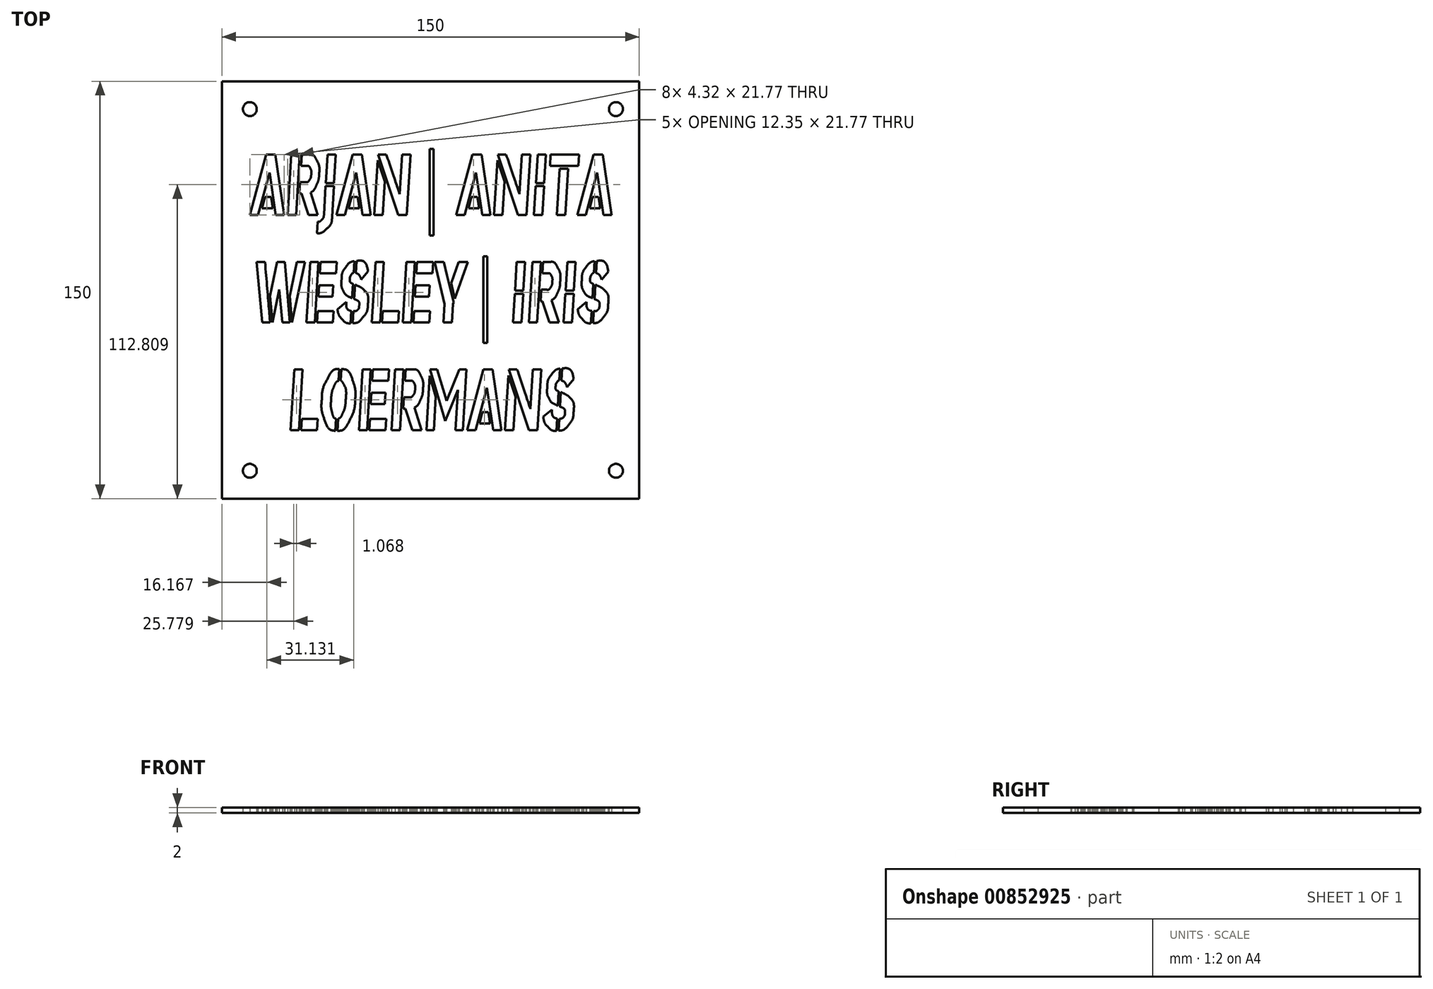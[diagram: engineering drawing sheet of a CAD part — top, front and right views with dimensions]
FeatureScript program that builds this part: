
annotation { "Feature Type Name" : "Feature", "Feature Type Description" : "" }
export const myFeature = defineFeature(function(context is Context, id is Id, definition is map)
    precondition{}
    {
        {
            var Q0;
            Q0=qCreatedBy(makeId("Top.planeOp"),FACE);
            var sketch = newSketch(context, id + "F0", { "sketchPlane" : qUnion([Q0])});
            skCircle(sketch, "E0", {"center": v(-65.05, 64.98) * mm, "radius": 2.5 * mm});
            skCircle(sketch, "E1", {"center": v(66.58, 64.98) * mm, "radius": 2.5 * mm});
            skCircle(sketch, "E2", {"center": v(-65.05, -65.02) * mm, "radius": 2.5 * mm});
            skCircle(sketch, "E3", {"center": v(66.58, -65.02) * mm, "radius": 2.5 * mm});
            skLineSegment(sketch, "E4.bottom", {"start": v(-75.05, 74.98) * mm, "end": v(74.95, 74.98) * mm});
            skLineSegment(sketch, "E4.top", {"start": v(-75.05, -75.02) * mm, "end": v(74.95, -75.02) * mm});
            skLineSegment(sketch, "E4.left", {"start": v(-75.05, 74.98) * mm, "end": v(-75.05, -75.02) * mm});
            skLineSegment(sketch, "E4.right", {"start": v(74.95, 74.98) * mm, "end": v(74.95, -75.02) * mm});
            skLineSegment(sketch, "E5", {"start": v(-62.06, 26.9) * mm, "end": v(-65.06, 26.9) * mm});
            skLineSegment(sketch, "E6", {"start": v(-65.06, 26.9) * mm, "end": v(-59.2, 48.68) * mm});
            skLineSegment(sketch, "E7", {"start": v(-59.2, 48.68) * mm, "end": v(-55.93, 48.68) * mm});
            skLineSegment(sketch, "E8", {"start": v(-55.93, 48.68) * mm, "end": v(-52.7, 26.9) * mm});
            skLineSegment(sketch, "E9", {"start": v(-52.7, 26.9) * mm, "end": v(-55.7, 26.9) * mm});
            skLineSegment(sketch, "E10", {"start": v(-55.7, 26.9) * mm, "end": v(-57.98, 42.11) * mm});
            skLineSegment(sketch, "E11", {"start": v(-57.98, 42.11) * mm, "end": v(-62.06, 26.9) * mm});
            skLineSegment(sketch, "E12", {"start": v(-60.66, 29.29) * mm, "end": v(-59.56, 33.36) * mm});
            skLineSegment(sketch, "E13", {"start": v(-59.56, 33.36) * mm, "end": v(-57.46, 33.36) * mm});
            skLineSegment(sketch, "E14", {"start": v(-57.46, 33.36) * mm, "end": v(-56.83, 29.29) * mm});
            skLineSegment(sketch, "E15", {"start": v(-56.83, 29.29) * mm, "end": v(-60.66, 29.29) * mm});
            skLineSegment(sketch, "E16", {"start": v(-40.6, 26.9) * mm, "end": v(-43.99, 26.9) * mm});
            skLineSegment(sketch, "E17", {"start": v(-43.99, 26.9) * mm, "end": v(-46.5, 34.62) * mm});
            skLineSegment(sketch, "E18", {"start": v(-46.5, 34.62) * mm, "end": v(-47.22, 34.62) * mm});
            skLineSegment(sketch, "E19", {"start": v(-47.22, 34.62) * mm, "end": v(-46.96, 38.7) * mm});
            skLineSegment(sketch, "E20", {"start": v(-46.96, 38.7) * mm, "end": v(-44.92, 38.7) * mm});
            skLineSegment(sketch, "E21", {"start": v(-44.57, 44.6) * mm, "end": v(-46.6, 44.6) * mm});
            skLineSegment(sketch, "E22", {"start": v(-46.6, 44.6) * mm, "end": v(-46.37, 48.68) * mm});
            skLineSegment(sketch, "E23", {"start": v(-46.37, 48.68) * mm, "end": v(-43.77, 48.68) * mm});
            skLineSegment(sketch, "E24", {"start": v(-43.23, 35) * mm, "end": v(-40.6, 26.9) * mm});
            skLineSegment(sketch, "E25", {"start": v(-48.43, 26.9) * mm, "end": v(-51.43, 26.9) * mm});
            skLineSegment(sketch, "E26", {"start": v(-51.43, 26.9) * mm, "end": v(-50.12, 48.68) * mm});
            skLineSegment(sketch, "E27", {"start": v(-50.12, 48.68) * mm, "end": v(-47.11, 48.68) * mm});
            skLineSegment(sketch, "E28", {"start": v(-47.11, 48.68) * mm, "end": v(-48.43, 26.9) * mm});
            skLineSegment(sketch, "E29", {"start": v(-34.77, 38.31) * mm, "end": v(-37.74, 38.31) * mm});
            skLineSegment(sketch, "E30", {"start": v(-37.74, 38.31) * mm, "end": v(-37.12, 48.7) * mm});
            skLineSegment(sketch, "E31", {"start": v(-37.12, 48.7) * mm, "end": v(-34.15, 48.7) * mm});
            skLineSegment(sketch, "E32", {"start": v(-34.15, 48.7) * mm, "end": v(-34.77, 38.31) * mm});
            skLineSegment(sketch, "E33", {"start": v(-34.83, 37.28) * mm, "end": v(-35.49, 26.3) * mm});
            skLineSegment(sketch, "E34", {"start": v(-40.93, 20.38) * mm, "end": v(-40.68, 24.52) * mm});
            skLineSegment(sketch, "E35", {"start": v(-38.42, 27.07) * mm, "end": v(-37.8, 37.28) * mm});
            skLineSegment(sketch, "E36", {"start": v(-37.8, 37.28) * mm, "end": v(-34.83, 37.28) * mm});
            skLineSegment(sketch, "E37", {"start": v(-30.93, 26.9) * mm, "end": v(-33.93, 26.9) * mm});
            skLineSegment(sketch, "E38", {"start": v(-33.93, 26.9) * mm, "end": v(-28.06, 48.68) * mm});
            skLineSegment(sketch, "E39", {"start": v(-28.06, 48.68) * mm, "end": v(-24.8, 48.68) * mm});
            skLineSegment(sketch, "E40", {"start": v(-24.8, 48.68) * mm, "end": v(-21.58, 26.9) * mm});
            skLineSegment(sketch, "E41", {"start": v(-21.58, 26.9) * mm, "end": v(-24.58, 26.9) * mm});
            skLineSegment(sketch, "E42", {"start": v(-24.58, 26.9) * mm, "end": v(-26.85, 42.11) * mm});
            skLineSegment(sketch, "E43", {"start": v(-26.85, 42.11) * mm, "end": v(-30.93, 26.9) * mm});
            skLineSegment(sketch, "E44", {"start": v(-29.53, 29.29) * mm, "end": v(-28.43, 33.36) * mm});
            skLineSegment(sketch, "E45", {"start": v(-28.43, 33.36) * mm, "end": v(-26.33, 33.36) * mm});
            skLineSegment(sketch, "E46", {"start": v(-26.33, 33.36) * mm, "end": v(-25.7, 29.29) * mm});
            skLineSegment(sketch, "E47", {"start": v(-25.7, 29.29) * mm, "end": v(-29.53, 29.29) * mm});
            skLineSegment(sketch, "E48", {"start": v(-16.57, 38.97) * mm, "end": v(-17.3, 26.9) * mm});
            skLineSegment(sketch, "E49", {"start": v(-17.3, 26.9) * mm, "end": v(-20.3, 26.9) * mm});
            skLineSegment(sketch, "E50", {"start": v(-20.3, 26.9) * mm, "end": v(-19.1, 46.56) * mm});
            skLineSegment(sketch, "E51", {"start": v(-19.1, 46.56) * mm, "end": v(-16.57, 38.97) * mm});
            skLineSegment(sketch, "E52", {"start": v(-8.62, 26.9) * mm, "end": v(-11.67, 26.9) * mm});
            skLineSegment(sketch, "E53", {"start": v(-11.67, 26.9) * mm, "end": v(-18.98, 48.68) * mm});
            skLineSegment(sketch, "E54", {"start": v(-18.98, 48.68) * mm, "end": v(-15.98, 48.68) * mm});
            skLineSegment(sketch, "E55", {"start": v(-11.17, 34.45) * mm, "end": v(-10.3, 48.68) * mm});
            skLineSegment(sketch, "E56", {"start": v(-10.3, 48.68) * mm, "end": v(-7.3, 48.68) * mm});
            skLineSegment(sketch, "E57", {"start": v(-7.3, 48.68) * mm, "end": v(-8.62, 26.9) * mm});
            skLineSegment(sketch, "E58", {"start": v(1.05, 50.68) * mm, "end": v(1.05, 19.56) * mm});
            skLineSegment(sketch, "E59", {"start": v(1.05, 19.56) * mm, "end": v(-0.43, 19.56) * mm});
            skLineSegment(sketch, "E60", {"start": v(-0.43, 19.56) * mm, "end": v(-0.43, 50.68) * mm});
            skLineSegment(sketch, "E61", {"start": v(-0.43, 50.68) * mm, "end": v(1.05, 50.68) * mm});
            skLineSegment(sketch, "E62", {"start": v(12.15, 26.9) * mm, "end": v(9.14, 26.9) * mm});
            skLineSegment(sketch, "E63", {"start": v(9.14, 26.9) * mm, "end": v(15, 48.68) * mm});
            skLineSegment(sketch, "E64", {"start": v(15, 48.68) * mm, "end": v(18.28, 48.68) * mm});
            skLineSegment(sketch, "E65", {"start": v(18.28, 48.68) * mm, "end": v(21.5, 26.9) * mm});
            skLineSegment(sketch, "E66", {"start": v(21.5, 26.9) * mm, "end": v(18.5, 26.9) * mm});
            skLineSegment(sketch, "E67", {"start": v(18.5, 26.9) * mm, "end": v(16.23, 42.11) * mm});
            skLineSegment(sketch, "E68", {"start": v(16.23, 42.11) * mm, "end": v(12.15, 26.9) * mm});
            skLineSegment(sketch, "E69", {"start": v(13.54, 29.29) * mm, "end": v(14.64, 33.36) * mm});
            skLineSegment(sketch, "E70", {"start": v(14.64, 33.36) * mm, "end": v(16.74, 33.36) * mm});
            skLineSegment(sketch, "E71", {"start": v(16.74, 33.36) * mm, "end": v(17.37, 29.29) * mm});
            skLineSegment(sketch, "E72", {"start": v(17.37, 29.29) * mm, "end": v(13.54, 29.29) * mm});
            skLineSegment(sketch, "E73", {"start": v(26.5, 38.97) * mm, "end": v(25.78, 26.9) * mm});
            skLineSegment(sketch, "E74", {"start": v(25.78, 26.9) * mm, "end": v(22.78, 26.9) * mm});
            skLineSegment(sketch, "E75", {"start": v(22.78, 26.9) * mm, "end": v(23.97, 46.56) * mm});
            skLineSegment(sketch, "E76", {"start": v(23.97, 46.56) * mm, "end": v(26.5, 38.97) * mm});
            skLineSegment(sketch, "E77", {"start": v(34.45, 26.9) * mm, "end": v(31.4, 26.9) * mm});
            skLineSegment(sketch, "E78", {"start": v(31.4, 26.9) * mm, "end": v(24.09, 48.68) * mm});
            skLineSegment(sketch, "E79", {"start": v(24.09, 48.68) * mm, "end": v(27.1, 48.68) * mm});
            skLineSegment(sketch, "E80", {"start": v(31.9, 34.45) * mm, "end": v(32.76, 48.68) * mm});
            skLineSegment(sketch, "E81", {"start": v(32.76, 48.68) * mm, "end": v(35.77, 48.68) * mm});
            skLineSegment(sketch, "E82", {"start": v(35.77, 48.68) * mm, "end": v(34.45, 26.9) * mm});
            skLineSegment(sketch, "E83", {"start": v(37.1, 26.9) * mm, "end": v(37.74, 37.28) * mm});
            skLineSegment(sketch, "E84", {"start": v(37.74, 37.28) * mm, "end": v(40.74, 37.28) * mm});
            skLineSegment(sketch, "E85", {"start": v(40.74, 37.28) * mm, "end": v(40.1, 26.9) * mm});
            skLineSegment(sketch, "E86", {"start": v(40.1, 26.9) * mm, "end": v(37.1, 26.9) * mm});
            skLineSegment(sketch, "E87", {"start": v(37.8, 38.31) * mm, "end": v(38.42, 48.68) * mm});
            skLineSegment(sketch, "E88", {"start": v(38.42, 48.68) * mm, "end": v(41.42, 48.68) * mm});
            skLineSegment(sketch, "E89", {"start": v(41.42, 48.68) * mm, "end": v(40.8, 38.31) * mm});
            skLineSegment(sketch, "E90", {"start": v(40.8, 38.31) * mm, "end": v(37.8, 38.31) * mm});
            skLineSegment(sketch, "E91", {"start": v(42.86, 44.6) * mm, "end": v(43.1, 48.68) * mm});
            skLineSegment(sketch, "E92", {"start": v(43.1, 48.68) * mm, "end": v(53.28, 48.68) * mm});
            skLineSegment(sketch, "E93", {"start": v(53.28, 48.68) * mm, "end": v(53.04, 44.6) * mm});
            skLineSegment(sketch, "E94", {"start": v(53.04, 44.6) * mm, "end": v(42.86, 44.6) * mm});
            skLineSegment(sketch, "E95", {"start": v(49.4, 43.52) * mm, "end": v(48.4, 26.9) * mm});
            skLineSegment(sketch, "E96", {"start": v(48.4, 26.9) * mm, "end": v(45.39, 26.9) * mm});
            skLineSegment(sketch, "E97", {"start": v(45.39, 26.9) * mm, "end": v(46.4, 43.52) * mm});
            skLineSegment(sketch, "E98", {"start": v(46.4, 43.52) * mm, "end": v(49.4, 43.52) * mm});
            skLineSegment(sketch, "E99", {"start": v(55.7, 26.9) * mm, "end": v(52.7, 26.9) * mm});
            skLineSegment(sketch, "E100", {"start": v(52.7, 26.9) * mm, "end": v(58.57, 48.68) * mm});
            skLineSegment(sketch, "E101", {"start": v(58.57, 48.68) * mm, "end": v(61.84, 48.68) * mm});
            skLineSegment(sketch, "E102", {"start": v(61.84, 48.68) * mm, "end": v(65.06, 26.9) * mm});
            skLineSegment(sketch, "E103", {"start": v(65.06, 26.9) * mm, "end": v(62.06, 26.9) * mm});
            skLineSegment(sketch, "E104", {"start": v(62.06, 26.9) * mm, "end": v(59.79, 42.11) * mm});
            skLineSegment(sketch, "E105", {"start": v(59.79, 42.11) * mm, "end": v(55.7, 26.9) * mm});
            skLineSegment(sketch, "E106", {"start": v(57.1, 29.29) * mm, "end": v(58.2, 33.36) * mm});
            skLineSegment(sketch, "E107", {"start": v(58.2, 33.36) * mm, "end": v(60.3, 33.36) * mm});
            skLineSegment(sketch, "E108", {"start": v(60.3, 33.36) * mm, "end": v(60.94, 29.29) * mm});
            skLineSegment(sketch, "E109", {"start": v(60.94, 29.29) * mm, "end": v(57.1, 29.29) * mm});
            skLineSegment(sketch, "E110", {"start": v(-50.63, -2.18) * mm, "end": v(-48.13, 10.04) * mm});
            skLineSegment(sketch, "E111", {"start": v(-48.13, 10.04) * mm, "end": v(-45.17, 10.04) * mm});
            skLineSegment(sketch, "E112", {"start": v(-45.17, 10.04) * mm, "end": v(-49.86, -11.74) * mm});
            skLineSegment(sketch, "E113", {"start": v(-49.86, -11.74) * mm, "end": v(-50.63, -2.18) * mm});
            skLineSegment(sketch, "E114", {"start": v(-50.61, -11.74) * mm, "end": v(-53.35, -11.74) * mm});
            skLineSegment(sketch, "E115", {"start": v(-53.35, -11.74) * mm, "end": v(-54.45, 0.05) * mm});
            skLineSegment(sketch, "E116", {"start": v(-54.45, 0.05) * mm, "end": v(-56.95, -11.74) * mm});
            skLineSegment(sketch, "E117", {"start": v(-56.95, -11.74) * mm, "end": v(-57.81, -2.18) * mm});
            skLineSegment(sketch, "E118", {"start": v(-57.81, -2.18) * mm, "end": v(-55.27, 10.04) * mm});
            skLineSegment(sketch, "E119", {"start": v(-55.27, 10.04) * mm, "end": v(-52.45, 10.04) * mm});
            skLineSegment(sketch, "E120", {"start": v(-52.45, 10.04) * mm, "end": v(-50.61, -11.74) * mm});
            skLineSegment(sketch, "E121", {"start": v(-60.52, -11.74) * mm, "end": v(-62.56, 10.04) * mm});
            skLineSegment(sketch, "E122", {"start": v(-62.56, 10.04) * mm, "end": v(-59.6, 10.04) * mm});
            skLineSegment(sketch, "E123", {"start": v(-57.78, -11.74) * mm, "end": v(-60.52, -11.74) * mm});
            skLineSegment(sketch, "E124", {"start": v(-41.68, -11.74) * mm, "end": v(-44.69, -11.74) * mm});
            skLineSegment(sketch, "E125", {"start": v(-44.69, -11.74) * mm, "end": v(-43.37, 10.04) * mm});
            skLineSegment(sketch, "E126", {"start": v(-43.37, 10.04) * mm, "end": v(-40.37, 10.04) * mm});
            skLineSegment(sketch, "E127", {"start": v(-40.37, 10.04) * mm, "end": v(-41.68, -11.74) * mm});
            skLineSegment(sketch, "E128", {"start": v(-40.13, 1.62) * mm, "end": v(-35.1, 1.62) * mm});
            skLineSegment(sketch, "E129", {"start": v(-35.1, 1.62) * mm, "end": v(-35.35, -2.45) * mm});
            skLineSegment(sketch, "E130", {"start": v(-35.35, -2.45) * mm, "end": v(-40.38, -2.45) * mm});
            skLineSegment(sketch, "E131", {"start": v(-40.38, -2.45) * mm, "end": v(-40.13, 1.62) * mm});
            skLineSegment(sketch, "E132", {"start": v(-40.7, -7.67) * mm, "end": v(-34.9, -7.67) * mm});
            skLineSegment(sketch, "E133", {"start": v(-34.9, -7.67) * mm, "end": v(-35.15, -11.74) * mm});
            skLineSegment(sketch, "E134", {"start": v(-35.15, -11.74) * mm, "end": v(-40.94, -11.74) * mm});
            skLineSegment(sketch, "E135", {"start": v(-40.94, -11.74) * mm, "end": v(-40.7, -7.67) * mm});
            skLineSegment(sketch, "E136", {"start": v(-39.63, 10.04) * mm, "end": v(-33.83, 10.04) * mm});
            skLineSegment(sketch, "E137", {"start": v(-33.83, 10.04) * mm, "end": v(-34.08, 5.96) * mm});
            skLineSegment(sketch, "E138", {"start": v(-34.08, 5.96) * mm, "end": v(-39.86, 5.96) * mm});
            skLineSegment(sketch, "E139", {"start": v(-39.86, 5.96) * mm, "end": v(-39.63, 10.04) * mm});
            skLineSegment(sketch, "E140", {"start": v(-27.95, 2.2) * mm, "end": v(-28.26, -2.97) * mm});
            skLineSegment(sketch, "E141", {"start": v(-27.45, 10.34) * mm, "end": v(-27.7, 6.1) * mm});
            skLineSegment(sketch, "E142", {"start": v(-26.7, 10.4) * mm, "end": v(-26.57, 10.4) * mm});
            skLineSegment(sketch, "E143", {"start": v(-22.56, 6.59) * mm, "end": v(-24.99, 3.72) * mm});
            skLineSegment(sketch, "E144", {"start": v(-26.96, 6.06) * mm, "end": v(-26.7, 10.4) * mm});
            skLineSegment(sketch, "E145", {"start": v(-27.21, 1.86) * mm, "end": v(-26.92, 1.76) * mm});
            skLineSegment(sketch, "E146", {"start": v(-28.04, -11.98) * mm, "end": v(-27.8, -7.7) * mm});
            skLineSegment(sketch, "E147", {"start": v(-27.8, -7.7) * mm, "end": v(-27.53, -7.7) * mm});
            skLineSegment(sketch, "E148", {"start": v(-27.51, -3.29) * mm, "end": v(-27.21, 1.86) * mm});
            skLineSegment(sketch, "E149", {"start": v(-33.53, -6.98) * mm, "end": v(-30.37, -4.38) * mm});
            skLineSegment(sketch, "E150", {"start": v(-28.54, -7.59) * mm, "end": v(-28.8, -12.04) * mm});
            skLineSegment(sketch, "E151", {"start": v(-17.23, -7.67) * mm, "end": v(-11.46, -7.67) * mm});
            skLineSegment(sketch, "E152", {"start": v(-11.46, -7.67) * mm, "end": v(-11.7, -11.74) * mm});
            skLineSegment(sketch, "E153", {"start": v(-11.7, -11.74) * mm, "end": v(-17.47, -11.74) * mm});
            skLineSegment(sketch, "E154", {"start": v(-17.47, -11.74) * mm, "end": v(-17.23, -7.67) * mm});
            skLineSegment(sketch, "E155", {"start": v(-18.19, -11.74) * mm, "end": v(-21.2, -11.74) * mm});
            skLineSegment(sketch, "E156", {"start": v(-21.2, -11.74) * mm, "end": v(-19.88, 10.04) * mm});
            skLineSegment(sketch, "E157", {"start": v(-19.88, 10.04) * mm, "end": v(-16.87, 10.04) * mm});
            skLineSegment(sketch, "E158", {"start": v(-16.87, 10.04) * mm, "end": v(-18.19, -11.74) * mm});
            skLineSegment(sketch, "E159", {"start": v(-7.02, -11.74) * mm, "end": v(-10.02, -11.74) * mm});
            skLineSegment(sketch, "E160", {"start": v(-10.02, -11.74) * mm, "end": v(-8.7, 10.04) * mm});
            skLineSegment(sketch, "E161", {"start": v(-8.7, 10.04) * mm, "end": v(-5.7, 10.04) * mm});
            skLineSegment(sketch, "E162", {"start": v(-5.7, 10.04) * mm, "end": v(-7.02, -11.74) * mm});
            skLineSegment(sketch, "E163", {"start": v(-5.46, 1.62) * mm, "end": v(-0.42, 1.62) * mm});
            skLineSegment(sketch, "E164", {"start": v(-0.42, 1.62) * mm, "end": v(-0.68, -2.45) * mm});
            skLineSegment(sketch, "E165", {"start": v(-0.68, -2.45) * mm, "end": v(-5.71, -2.45) * mm});
            skLineSegment(sketch, "E166", {"start": v(-5.71, -2.45) * mm, "end": v(-5.46, 1.62) * mm});
            skLineSegment(sketch, "E167", {"start": v(-6.03, -7.67) * mm, "end": v(-0.24, -7.67) * mm});
            skLineSegment(sketch, "E168", {"start": v(-0.24, -7.67) * mm, "end": v(-0.48, -11.74) * mm});
            skLineSegment(sketch, "E169", {"start": v(-0.48, -11.74) * mm, "end": v(-6.27, -11.74) * mm});
            skLineSegment(sketch, "E170", {"start": v(-6.27, -11.74) * mm, "end": v(-6.03, -7.67) * mm});
            skLineSegment(sketch, "E171", {"start": v(-4.96, 10.04) * mm, "end": v(0.84, 10.04) * mm});
            skLineSegment(sketch, "E172", {"start": v(0.84, 10.04) * mm, "end": v(0.6, 5.96) * mm});
            skLineSegment(sketch, "E173", {"start": v(0.6, 5.96) * mm, "end": v(-5.2, 5.96) * mm});
            skLineSegment(sketch, "E174", {"start": v(-5.2, 5.96) * mm, "end": v(-4.96, 10.04) * mm});
            skLineSegment(sketch, "E175", {"start": v(5, -5.14) * mm, "end": v(1.41, 10.04) * mm});
            skLineSegment(sketch, "E176", {"start": v(1.41, 10.04) * mm, "end": v(4.68, 10.04) * mm});
            skLineSegment(sketch, "E177", {"start": v(4.68, 10.04) * mm, "end": v(5.83, 5.23) * mm});
            skLineSegment(sketch, "E178", {"start": v(5.83, 5.23) * mm, "end": v(8.2, -4.5) * mm});
            skLineSegment(sketch, "E179", {"start": v(8.2, -4.5) * mm, "end": v(7.97, -5.14) * mm});
            skLineSegment(sketch, "E180", {"start": v(7.97, -5.14) * mm, "end": v(7.57, -11.74) * mm});
            skLineSegment(sketch, "E181", {"start": v(7.57, -11.74) * mm, "end": v(4.6, -11.74) * mm});
            skLineSegment(sketch, "E182", {"start": v(4.6, -11.74) * mm, "end": v(5, -5.14) * mm});
            skLineSegment(sketch, "E183", {"start": v(7.34, 2.36) * mm, "end": v(10.09, 10.04) * mm});
            skLineSegment(sketch, "E184", {"start": v(10.09, 10.04) * mm, "end": v(13.4, 10.04) * mm});
            skLineSegment(sketch, "E185", {"start": v(13.4, 10.04) * mm, "end": v(8.65, -3.2) * mm});
            skLineSegment(sketch, "E186", {"start": v(8.65, -3.2) * mm, "end": v(7.34, 2.36) * mm});
            skLineSegment(sketch, "E187", {"start": v(20.37, 12.04) * mm, "end": v(20.37, -19.08) * mm});
            skLineSegment(sketch, "E188", {"start": v(20.37, -19.08) * mm, "end": v(18.88, -19.08) * mm});
            skLineSegment(sketch, "E189", {"start": v(18.88, -19.08) * mm, "end": v(18.88, 12.04) * mm});
            skLineSegment(sketch, "E190", {"start": v(18.88, 12.04) * mm, "end": v(20.37, 12.04) * mm});
            skLineSegment(sketch, "E191", {"start": v(29.6, -11.74) * mm, "end": v(30.23, -1.36) * mm});
            skLineSegment(sketch, "E192", {"start": v(30.23, -1.36) * mm, "end": v(33.23, -1.36) * mm});
            skLineSegment(sketch, "E193", {"start": v(33.23, -1.36) * mm, "end": v(32.6, -11.74) * mm});
            skLineSegment(sketch, "E194", {"start": v(32.6, -11.74) * mm, "end": v(29.6, -11.74) * mm});
            skLineSegment(sketch, "E195", {"start": v(30.29, -0.33) * mm, "end": v(30.9, 10.04) * mm});
            skLineSegment(sketch, "E196", {"start": v(30.9, 10.04) * mm, "end": v(33.91, 10.04) * mm});
            skLineSegment(sketch, "E197", {"start": v(33.91, 10.04) * mm, "end": v(33.29, -0.33) * mm});
            skLineSegment(sketch, "E198", {"start": v(33.29, -0.33) * mm, "end": v(30.29, -0.33) * mm});
            skLineSegment(sketch, "E199", {"start": v(46.08, -11.74) * mm, "end": v(42.7, -11.74) * mm});
            skLineSegment(sketch, "E200", {"start": v(42.7, -11.74) * mm, "end": v(40.19, -4.02) * mm});
            skLineSegment(sketch, "E201", {"start": v(40.19, -4.02) * mm, "end": v(39.47, -4.02) * mm});
            skLineSegment(sketch, "E202", {"start": v(39.47, -4.02) * mm, "end": v(39.72, 0.05) * mm});
            skLineSegment(sketch, "E203", {"start": v(39.72, 0.05) * mm, "end": v(41.76, 0.05) * mm});
            skLineSegment(sketch, "E204", {"start": v(42.12, 5.96) * mm, "end": v(40.08, 5.96) * mm});
            skLineSegment(sketch, "E205", {"start": v(40.08, 5.96) * mm, "end": v(40.32, 10.04) * mm});
            skLineSegment(sketch, "E206", {"start": v(40.32, 10.04) * mm, "end": v(42.92, 10.04) * mm});
            skLineSegment(sketch, "E207", {"start": v(43.45, -3.64) * mm, "end": v(46.08, -11.74) * mm});
            skLineSegment(sketch, "E208", {"start": v(38.26, -11.74) * mm, "end": v(35.26, -11.74) * mm});
            skLineSegment(sketch, "E209", {"start": v(35.26, -11.74) * mm, "end": v(36.57, 10.04) * mm});
            skLineSegment(sketch, "E210", {"start": v(36.57, 10.04) * mm, "end": v(39.58, 10.04) * mm});
            skLineSegment(sketch, "E211", {"start": v(39.58, 10.04) * mm, "end": v(38.26, -11.74) * mm});
            skLineSegment(sketch, "E212", {"start": v(47.8, -11.74) * mm, "end": v(48.43, -1.36) * mm});
            skLineSegment(sketch, "E213", {"start": v(48.43, -1.36) * mm, "end": v(51.44, -1.36) * mm});
            skLineSegment(sketch, "E214", {"start": v(51.44, -1.36) * mm, "end": v(50.8, -11.74) * mm});
            skLineSegment(sketch, "E215", {"start": v(50.8, -11.74) * mm, "end": v(47.8, -11.74) * mm});
            skLineSegment(sketch, "E216", {"start": v(48.5, -0.33) * mm, "end": v(49.12, 10.04) * mm});
            skLineSegment(sketch, "E217", {"start": v(49.12, 10.04) * mm, "end": v(52.12, 10.04) * mm});
            skLineSegment(sketch, "E218", {"start": v(52.12, 10.04) * mm, "end": v(51.5, -0.33) * mm});
            skLineSegment(sketch, "E219", {"start": v(51.5, -0.33) * mm, "end": v(48.5, -0.33) * mm});
            skLineSegment(sketch, "E220", {"start": v(58.44, 2.2) * mm, "end": v(58.13, -2.97) * mm});
            skLineSegment(sketch, "E221", {"start": v(58.94, 10.34) * mm, "end": v(58.69, 6.1) * mm});
            skLineSegment(sketch, "E222", {"start": v(59.7, 10.4) * mm, "end": v(59.82, 10.4) * mm});
            skLineSegment(sketch, "E223", {"start": v(63.83, 6.59) * mm, "end": v(61.4, 3.72) * mm});
            skLineSegment(sketch, "E224", {"start": v(59.43, 6.06) * mm, "end": v(59.7, 10.4) * mm});
            skLineSegment(sketch, "E225", {"start": v(59.18, 1.86) * mm, "end": v(59.47, 1.76) * mm});
            skLineSegment(sketch, "E226", {"start": v(58.35, -11.98) * mm, "end": v(58.6, -7.7) * mm});
            skLineSegment(sketch, "E227", {"start": v(58.6, -7.7) * mm, "end": v(58.86, -7.7) * mm});
            skLineSegment(sketch, "E228", {"start": v(58.88, -3.29) * mm, "end": v(59.18, 1.86) * mm});
            skLineSegment(sketch, "E229", {"start": v(52.86, -6.98) * mm, "end": v(56.02, -4.38) * mm});
            skLineSegment(sketch, "E230", {"start": v(57.85, -7.59) * mm, "end": v(57.58, -12.04) * mm});
            skLineSegment(sketch, "E231", {"start": v(-46.4, -46.3) * mm, "end": v(-40.63, -46.3) * mm});
            skLineSegment(sketch, "E232", {"start": v(-40.63, -46.3) * mm, "end": v(-40.86, -50.38) * mm});
            skLineSegment(sketch, "E233", {"start": v(-40.86, -50.38) * mm, "end": v(-46.64, -50.38) * mm});
            skLineSegment(sketch, "E234", {"start": v(-46.64, -50.38) * mm, "end": v(-46.4, -46.3) * mm});
            skLineSegment(sketch, "E235", {"start": v(-47.36, -50.38) * mm, "end": v(-50.36, -50.38) * mm});
            skLineSegment(sketch, "E236", {"start": v(-50.36, -50.38) * mm, "end": v(-49.05, -28.6) * mm});
            skLineSegment(sketch, "E237", {"start": v(-49.05, -28.6) * mm, "end": v(-46.04, -28.6) * mm});
            skLineSegment(sketch, "E238", {"start": v(-46.04, -28.6) * mm, "end": v(-47.36, -50.38) * mm});
            skLineSegment(sketch, "E239", {"start": v(-32.9, -28.47) * mm, "end": v(-33.16, -32.7) * mm});
            skLineSegment(sketch, "E240", {"start": v(-33.98, -46.3) * mm, "end": v(-34.24, -50.64) * mm});
            skLineSegment(sketch, "E241", {"start": v(-32.4, -32.65) * mm, "end": v(-32.15, -28.47) * mm});
            skLineSegment(sketch, "E242", {"start": v(-33.48, -50.64) * mm, "end": v(-33.22, -46.3) * mm});
            skLineSegment(sketch, "E243", {"start": v(-22.85, -50.38) * mm, "end": v(-25.85, -50.38) * mm});
            skLineSegment(sketch, "E244", {"start": v(-25.85, -50.38) * mm, "end": v(-24.53, -28.6) * mm});
            skLineSegment(sketch, "E245", {"start": v(-24.53, -28.6) * mm, "end": v(-21.53, -28.6) * mm});
            skLineSegment(sketch, "E246", {"start": v(-21.53, -28.6) * mm, "end": v(-22.85, -50.38) * mm});
            skLineSegment(sketch, "E247", {"start": v(-21.29, -37.02) * mm, "end": v(-16.25, -37.02) * mm});
            skLineSegment(sketch, "E248", {"start": v(-16.25, -37.02) * mm, "end": v(-16.5, -41.1) * mm});
            skLineSegment(sketch, "E249", {"start": v(-16.5, -41.1) * mm, "end": v(-21.54, -41.1) * mm});
            skLineSegment(sketch, "E250", {"start": v(-21.54, -41.1) * mm, "end": v(-21.29, -37.02) * mm});
            skLineSegment(sketch, "E251", {"start": v(-21.86, -46.3) * mm, "end": v(-16.07, -46.3) * mm});
            skLineSegment(sketch, "E252", {"start": v(-16.07, -46.3) * mm, "end": v(-16.3, -50.38) * mm});
            skLineSegment(sketch, "E253", {"start": v(-16.3, -50.38) * mm, "end": v(-22.1, -50.38) * mm});
            skLineSegment(sketch, "E254", {"start": v(-22.1, -50.38) * mm, "end": v(-21.86, -46.3) * mm});
            skLineSegment(sketch, "E255", {"start": v(-20.79, -28.6) * mm, "end": v(-15, -28.6) * mm});
            skLineSegment(sketch, "E256", {"start": v(-15, -28.6) * mm, "end": v(-15.24, -32.68) * mm});
            skLineSegment(sketch, "E257", {"start": v(-15.24, -32.68) * mm, "end": v(-21.02, -32.68) * mm});
            skLineSegment(sketch, "E258", {"start": v(-21.02, -32.68) * mm, "end": v(-20.79, -28.6) * mm});
            skLineSegment(sketch, "E259", {"start": v(-3.26, -50.38) * mm, "end": v(-6.64, -50.38) * mm});
            skLineSegment(sketch, "E260", {"start": v(-6.64, -50.38) * mm, "end": v(-9.15, -42.66) * mm});
            skLineSegment(sketch, "E261", {"start": v(-9.15, -42.66) * mm, "end": v(-9.87, -42.66) * mm});
            skLineSegment(sketch, "E262", {"start": v(-9.87, -42.66) * mm, "end": v(-9.62, -38.59) * mm});
            skLineSegment(sketch, "E263", {"start": v(-9.62, -38.59) * mm, "end": v(-7.58, -38.59) * mm});
            skLineSegment(sketch, "E264", {"start": v(-7.22, -32.68) * mm, "end": v(-9.26, -32.68) * mm});
            skLineSegment(sketch, "E265", {"start": v(-9.26, -32.68) * mm, "end": v(-9.02, -28.6) * mm});
            skLineSegment(sketch, "E266", {"start": v(-9.02, -28.6) * mm, "end": v(-6.42, -28.6) * mm});
            skLineSegment(sketch, "E267", {"start": v(-5.89, -42.28) * mm, "end": v(-3.26, -50.38) * mm});
            skLineSegment(sketch, "E268", {"start": v(-11.08, -50.38) * mm, "end": v(-14.08, -50.38) * mm});
            skLineSegment(sketch, "E269", {"start": v(-14.08, -50.38) * mm, "end": v(-12.77, -28.6) * mm});
            skLineSegment(sketch, "E270", {"start": v(-12.77, -28.6) * mm, "end": v(-9.77, -28.6) * mm});
            skLineSegment(sketch, "E271", {"start": v(-9.77, -28.6) * mm, "end": v(-11.08, -50.38) * mm});
            skLineSegment(sketch, "E272", {"start": v(-0.23, -28.6) * mm, "end": v(2.32, -28.6) * mm});
            skLineSegment(sketch, "E273", {"start": v(2.32, -28.6) * mm, "end": v(5.67, -39.85) * mm});
            skLineSegment(sketch, "E274", {"start": v(5.67, -39.85) * mm, "end": v(10.32, -28.6) * mm});
            skLineSegment(sketch, "E275", {"start": v(10.32, -28.6) * mm, "end": v(12.88, -28.6) * mm});
            skLineSegment(sketch, "E276", {"start": v(12.88, -28.6) * mm, "end": v(11.57, -50.38) * mm});
            skLineSegment(sketch, "E277", {"start": v(11.57, -50.38) * mm, "end": v(8.93, -50.38) * mm});
            skLineSegment(sketch, "E278", {"start": v(8.93, -50.38) * mm, "end": v(9.8, -35.99) * mm});
            skLineSegment(sketch, "E279", {"start": v(9.8, -35.99) * mm, "end": v(5.23, -47.13) * mm});
            skLineSegment(sketch, "E280", {"start": v(5.23, -47.13) * mm, "end": v(-0.23, -28.6) * mm});
            skLineSegment(sketch, "E281", {"start": v(1.8, -38.31) * mm, "end": v(1.08, -50.38) * mm});
            skLineSegment(sketch, "E282", {"start": v(1.08, -50.38) * mm, "end": v(-1.55, -50.38) * mm});
            skLineSegment(sketch, "E283", {"start": v(-1.55, -50.38) * mm, "end": v(-0.37, -30.93) * mm});
            skLineSegment(sketch, "E284", {"start": v(-0.37, -30.93) * mm, "end": v(1.8, -38.31) * mm});
            skLineSegment(sketch, "E285", {"start": v(16.09, -50.38) * mm, "end": v(13.08, -50.38) * mm});
            skLineSegment(sketch, "E286", {"start": v(13.08, -50.38) * mm, "end": v(18.95, -28.6) * mm});
            skLineSegment(sketch, "E287", {"start": v(18.95, -28.6) * mm, "end": v(22.21, -28.6) * mm});
            skLineSegment(sketch, "E288", {"start": v(22.21, -28.6) * mm, "end": v(25.44, -50.38) * mm});
            skLineSegment(sketch, "E289", {"start": v(25.44, -50.38) * mm, "end": v(22.43, -50.38) * mm});
            skLineSegment(sketch, "E290", {"start": v(22.43, -50.38) * mm, "end": v(20.17, -35.17) * mm});
            skLineSegment(sketch, "E291", {"start": v(20.17, -35.17) * mm, "end": v(16.09, -50.38) * mm});
            skLineSegment(sketch, "E292", {"start": v(17.48, -48) * mm, "end": v(18.58, -43.92) * mm});
            skLineSegment(sketch, "E293", {"start": v(18.58, -43.92) * mm, "end": v(20.68, -43.92) * mm});
            skLineSegment(sketch, "E294", {"start": v(20.68, -43.92) * mm, "end": v(21.31, -48) * mm});
            skLineSegment(sketch, "E295", {"start": v(21.31, -48) * mm, "end": v(17.48, -48) * mm});
            skLineSegment(sketch, "E296", {"start": v(30.44, -38.31) * mm, "end": v(29.72, -50.38) * mm});
            skLineSegment(sketch, "E297", {"start": v(29.72, -50.38) * mm, "end": v(26.71, -50.38) * mm});
            skLineSegment(sketch, "E298", {"start": v(26.71, -50.38) * mm, "end": v(27.9, -30.72) * mm});
            skLineSegment(sketch, "E299", {"start": v(27.9, -30.72) * mm, "end": v(30.44, -38.31) * mm});
            skLineSegment(sketch, "E300", {"start": v(38.4, -50.38) * mm, "end": v(35.35, -50.38) * mm});
            skLineSegment(sketch, "E301", {"start": v(35.35, -50.38) * mm, "end": v(28.03, -28.6) * mm});
            skLineSegment(sketch, "E302", {"start": v(28.03, -28.6) * mm, "end": v(31.03, -28.6) * mm});
            skLineSegment(sketch, "E303", {"start": v(35.85, -42.83) * mm, "end": v(36.7, -28.6) * mm});
            skLineSegment(sketch, "E304", {"start": v(36.7, -28.6) * mm, "end": v(39.7, -28.6) * mm});
            skLineSegment(sketch, "E305", {"start": v(39.7, -28.6) * mm, "end": v(38.4, -50.38) * mm});
            skLineSegment(sketch, "E306", {"start": v(46, -36.44) * mm, "end": v(45.7, -41.61) * mm});
            skLineSegment(sketch, "E307", {"start": v(46.5, -28.3) * mm, "end": v(46.25, -32.54) * mm});
            skLineSegment(sketch, "E308", {"start": v(47.26, -28.24) * mm, "end": v(47.4, -28.24) * mm});
            skLineSegment(sketch, "E309", {"start": v(51.4, -32.05) * mm, "end": v(48.97, -34.92) * mm});
            skLineSegment(sketch, "E310", {"start": v(47, -32.58) * mm, "end": v(47.26, -28.24) * mm});
            skLineSegment(sketch, "E311", {"start": v(46.75, -36.78) * mm, "end": v(47.04, -36.88) * mm});
            skLineSegment(sketch, "E312", {"start": v(45.92, -50.62) * mm, "end": v(46.17, -46.34) * mm});
            skLineSegment(sketch, "E313", {"start": v(46.17, -46.34) * mm, "end": v(46.43, -46.34) * mm});
            skLineSegment(sketch, "E314", {"start": v(46.45, -41.93) * mm, "end": v(46.75, -36.78) * mm});
            skLineSegment(sketch, "E315", {"start": v(40.42, -45.62) * mm, "end": v(43.58, -43.02) * mm});
            skLineSegment(sketch, "E316", {"start": v(45.42, -46.23) * mm, "end": v(45.15, -50.68) * mm});
            skFitSpline(sketch, "E317", {"points": [v(-44.92, 38.7) * mm, v(-44.4, 38.7) * mm, v(-43.95, 38.97) * mm, v(-43.6, 39.53) * mm]});
            skFitSpline(sketch, "E318", {"points": [v(-43.6, 39.53) * mm, v(-43.24, 40.08) * mm, v(-43.03, 40.78) * mm, v(-42.98, 41.64) * mm]});
            skFitSpline(sketch, "E319", {"points": [v(-42.98, 41.64) * mm, v(-42.93, 42.47) * mm, v(-43.05, 43.17) * mm, v(-43.34, 43.74) * mm]});
            skFitSpline(sketch, "E320", {"points": [v(-43.34, 43.74) * mm, v(-43.64, 44.32) * mm, v(-44.05, 44.6) * mm, v(-44.57, 44.6) * mm]});
            skFitSpline(sketch, "E321", {"points": [v(-43.77, 48.68) * mm, v(-42.68, 48.68) * mm, v(-41.77, 47.99) * mm, v(-41.05, 46.6) * mm]});
            skFitSpline(sketch, "E322", {"points": [v(-41.05, 46.6) * mm, v(-40.33, 45.22) * mm, v(-40.02, 43.6) * mm, v(-40.14, 41.75) * mm]});
            skFitSpline(sketch, "E323", {"points": [v(-40.14, 41.75) * mm, v(-40.23, 40.18) * mm, v(-40.57, 38.78) * mm, v(-41.13, 37.57) * mm]});
            skFitSpline(sketch, "E324", {"points": [v(-41.13, 37.57) * mm, v(-41.68, 36.34) * mm, v(-42.38, 35.49) * mm, v(-43.23, 35) * mm]});
            skFitSpline(sketch, "E325", {"points": [v(-35.49, 26.3) * mm, v(-35.6, 24.57) * mm, v(-36.27, 23.1) * mm, v(-37.47, 21.93) * mm]});
            skFitSpline(sketch, "E326", {"points": [v(-37.47, 21.93) * mm, v(-38.56, 20.9) * mm, v(-39.71, 20.38) * mm, v(-40.93, 20.38) * mm]});
            skFitSpline(sketch, "E327", {"points": [v(-40.68, 24.52) * mm, v(-40.11, 24.52) * mm, v(-39.6, 24.75) * mm, v(-39.15, 25.23) * mm]});
            skFitSpline(sketch, "E328", {"points": [v(-39.15, 25.23) * mm, v(-38.7, 25.74) * mm, v(-38.46, 26.35) * mm, v(-38.42, 27.07) * mm]});
            skFitSpline(sketch, "E329", {"points": [v(-15.98, 48.68) * mm, v(-13.15, 40.33) * mm, v(-11.55, 35.59) * mm, v(-11.17, 34.45) * mm]});
            skFitSpline(sketch, "E330", {"points": [v(27.1, 48.68) * mm, v(29.92, 40.33) * mm, v(31.53, 35.59) * mm, v(31.9, 34.45) * mm]});
            skFitSpline(sketch, "E331", {"points": [v(-59.6, 10.04) * mm, v(-58.54, -2.34) * mm, v(-57.94, -9.6) * mm, v(-57.78, -11.74) * mm]});
            skFitSpline(sketch, "E332", {"points": [v(-27.7, 6.1) * mm, v(-28.07, 6) * mm, v(-28.38, 5.75) * mm, v(-28.64, 5.33) * mm]});
            skFitSpline(sketch, "E333", {"points": [v(-28.64, 5.33) * mm, v(-28.9, 4.91) * mm, v(-29.04, 4.47) * mm, v(-29.06, 4.02) * mm]});
            skFitSpline(sketch, "E334", {"points": [v(-29.06, 4.02) * mm, v(-29.11, 3.14) * mm, v(-28.74, 2.53) * mm, v(-27.95, 2.2) * mm]});
            skFitSpline(sketch, "E335", {"points": [v(-28.26, -2.97) * mm, v(-29.85, -2.26) * mm, v(-30.88, -1.43) * mm, v(-31.37, -0.46) * mm]});
            skFitSpline(sketch, "E336", {"points": [v(-31.37, -0.46) * mm, v(-31.93, 0.62) * mm, v(-32.16, 2.01) * mm, v(-32.05, 3.72) * mm]});
            skFitSpline(sketch, "E337", {"points": [v(-32.05, 3.72) * mm, v(-31.95, 5.48) * mm, v(-31.44, 6.97) * mm, v(-30.52, 8.2) * mm]});
            skFitSpline(sketch, "E338", {"points": [v(-30.52, 8.2) * mm, v(-29.66, 9.34) * mm, v(-28.64, 10.06) * mm, v(-27.45, 10.34) * mm]});
            skFitSpline(sketch, "E339", {"points": [v(-26.57, 10.4) * mm, v(-24.55, 10.4) * mm, v(-23.21, 9.13) * mm, v(-22.56, 6.59) * mm]});
            skFitSpline(sketch, "E340", {"points": [v(-24.99, 3.72) * mm, v(-25.43, 4.88) * mm, v(-26.1, 5.66) * mm, v(-26.96, 6.06) * mm]});
            skFitSpline(sketch, "E341", {"points": [v(-26.92, 1.76) * mm, v(-25.4, 1.04) * mm, v(-24.38, 0.38) * mm, v(-23.85, -0.2) * mm]});
            skFitSpline(sketch, "E342", {"points": [v(-23.85, -0.2) * mm, v(-22.88, -1.3) * mm, v(-22.46, -2.94) * mm, v(-22.6, -5.08) * mm]});
            skFitSpline(sketch, "E343", {"points": [v(-22.6, -5.08) * mm, v(-22.73, -6.95) * mm, v(-23.31, -8.52) * mm, v(-24.35, -9.8) * mm]});
            skFitSpline(sketch, "E344", {"points": [v(-24.35, -9.8) * mm, v(-25.38, -11.07) * mm, v(-26.6, -11.8) * mm, v(-28.04, -11.98) * mm]});
            skFitSpline(sketch, "E345", {"points": [v(-27.53, -7.7) * mm, v(-26.99, -7.62) * mm, v(-26.57, -7.42) * mm, v(-26.27, -7.12) * mm]});
            skFitSpline(sketch, "E346", {"points": [v(-26.27, -7.12) * mm, v(-25.95, -6.8) * mm, v(-25.78, -6.39) * mm, v(-25.75, -5.9) * mm]});
            skFitSpline(sketch, "E347", {"points": [v(-25.75, -5.9) * mm, v(-25.68, -4.75) * mm, v(-26.17, -3.93) * mm, v(-27.23, -3.44) * mm]});
            skFitSpline(sketch, "E348", {"points": [v(-27.23, -3.44) * mm, v(-27.41, -3.35) * mm, v(-27.5, -3.3) * mm, v(-27.51, -3.29) * mm]});
            skFitSpline(sketch, "E349", {"points": [v(-28.8, -12.04) * mm, v(-29.97, -11.97) * mm, v(-30.99, -11.48) * mm, v(-31.84, -10.57) * mm]});
            skFitSpline(sketch, "E350", {"points": [v(-31.84, -10.57) * mm, v(-32.69, -9.67) * mm, v(-33.25, -8.47) * mm, v(-33.53, -6.98) * mm]});
            skFitSpline(sketch, "E351", {"points": [v(-30.37, -4.38) * mm, v(-30.32, -6.1) * mm, v(-29.7, -7.17) * mm, v(-28.54, -7.59) * mm]});
            skFitSpline(sketch, "E352", {"points": [v(41.76, 0.05) * mm, v(42.3, 0.05) * mm, v(42.74, 0.33) * mm, v(43.1, 0.89) * mm]});
            skFitSpline(sketch, "E353", {"points": [v(43.1, 0.89) * mm, v(43.45, 1.44) * mm, v(43.65, 2.14) * mm, v(43.7, 3) * mm]});
            skFitSpline(sketch, "E354", {"points": [v(43.7, 3) * mm, v(43.75, 3.83) * mm, v(43.63, 4.53) * mm, v(43.35, 5.1) * mm]});
            skFitSpline(sketch, "E355", {"points": [v(43.35, 5.1) * mm, v(43.04, 5.68) * mm, v(42.64, 5.96) * mm, v(42.12, 5.96) * mm]});
            skFitSpline(sketch, "E356", {"points": [v(42.92, 10.04) * mm, v(44.01, 10.04) * mm, v(44.92, 9.35) * mm, v(45.64, 7.97) * mm]});
            skFitSpline(sketch, "E357", {"points": [v(45.64, 7.97) * mm, v(46.36, 6.58) * mm, v(46.66, 4.96) * mm, v(46.55, 3.1) * mm]});
            skFitSpline(sketch, "E358", {"points": [v(46.55, 3.1) * mm, v(46.45, 1.54) * mm, v(46.12, 0.14) * mm, v(45.55, -1.07) * mm]});
            skFitSpline(sketch, "E359", {"points": [v(45.55, -1.07) * mm, v(45, -2.3) * mm, v(44.3, -3.15) * mm, v(43.45, -3.64) * mm]});
            skFitSpline(sketch, "E360", {"points": [v(58.69, 6.1) * mm, v(58.32, 6) * mm, v(58.01, 5.75) * mm, v(57.75, 5.33) * mm]});
            skFitSpline(sketch, "E361", {"points": [v(57.75, 5.33) * mm, v(57.5, 4.91) * mm, v(57.35, 4.47) * mm, v(57.33, 4.02) * mm]});
            skFitSpline(sketch, "E362", {"points": [v(57.33, 4.02) * mm, v(57.28, 3.14) * mm, v(57.65, 2.53) * mm, v(58.44, 2.2) * mm]});
            skFitSpline(sketch, "E363", {"points": [v(58.13, -2.97) * mm, v(56.54, -2.26) * mm, v(55.5, -1.43) * mm, v(55.02, -0.46) * mm]});
            skFitSpline(sketch, "E364", {"points": [v(55.02, -0.46) * mm, v(54.46, 0.62) * mm, v(54.23, 2.01) * mm, v(54.34, 3.72) * mm]});
            skFitSpline(sketch, "E365", {"points": [v(54.34, 3.72) * mm, v(54.44, 5.48) * mm, v(54.95, 6.97) * mm, v(55.87, 8.2) * mm]});
            skFitSpline(sketch, "E366", {"points": [v(55.87, 8.2) * mm, v(56.73, 9.34) * mm, v(57.75, 10.06) * mm, v(58.94, 10.34) * mm]});
            skFitSpline(sketch, "E367", {"points": [v(59.82, 10.4) * mm, v(61.84, 10.4) * mm, v(63.18, 9.13) * mm, v(63.83, 6.59) * mm]});
            skFitSpline(sketch, "E368", {"points": [v(61.4, 3.72) * mm, v(60.96, 4.88) * mm, v(60.3, 5.66) * mm, v(59.43, 6.06) * mm]});
            skFitSpline(sketch, "E369", {"points": [v(59.47, 1.76) * mm, v(60.99, 1.04) * mm, v(62, 0.38) * mm, v(62.54, -0.2) * mm]});
            skFitSpline(sketch, "E370", {"points": [v(62.54, -0.2) * mm, v(63.51, -1.3) * mm, v(63.93, -2.94) * mm, v(63.8, -5.08) * mm]});
            skFitSpline(sketch, "E371", {"points": [v(63.8, -5.08) * mm, v(63.66, -6.95) * mm, v(63.08, -8.52) * mm, v(62.04, -9.8) * mm]});
            skFitSpline(sketch, "E372", {"points": [v(62.04, -9.8) * mm, v(61.01, -11.07) * mm, v(59.78, -11.8) * mm, v(58.35, -11.98) * mm]});
            skFitSpline(sketch, "E373", {"points": [v(58.86, -7.7) * mm, v(59.4, -7.62) * mm, v(59.82, -7.42) * mm, v(60.12, -7.12) * mm]});
            skFitSpline(sketch, "E374", {"points": [v(60.12, -7.12) * mm, v(60.44, -6.8) * mm, v(60.6, -6.39) * mm, v(60.64, -5.9) * mm]});
            skFitSpline(sketch, "E375", {"points": [v(60.64, -5.9) * mm, v(60.7, -4.75) * mm, v(60.22, -3.93) * mm, v(59.16, -3.44) * mm]});
            skFitSpline(sketch, "E376", {"points": [v(59.16, -3.44) * mm, v(58.98, -3.35) * mm, v(58.88, -3.3) * mm, v(58.88, -3.29) * mm]});
            skFitSpline(sketch, "E377", {"points": [v(57.58, -12.04) * mm, v(56.42, -11.97) * mm, v(55.4, -11.48) * mm, v(54.55, -10.57) * mm]});
            skFitSpline(sketch, "E378", {"points": [v(54.55, -10.57) * mm, v(53.7, -9.67) * mm, v(53.14, -8.47) * mm, v(52.86, -6.98) * mm]});
            skFitSpline(sketch, "E379", {"points": [v(56.02, -4.38) * mm, v(56.07, -6.1) * mm, v(56.69, -7.17) * mm, v(57.85, -7.59) * mm]});
            skFitSpline(sketch, "E380", {"points": [v(-34.24, -50.64) * mm, v(-36, -50.32) * mm, v(-37.38, -48.8) * mm, v(-38.4, -46.06) * mm]});
            skFitSpline(sketch, "E381", {"points": [v(-38.4, -46.06) * mm, v(-39.07, -44) * mm, v(-39.33, -41.8) * mm, v(-39.18, -39.47) * mm]});
            skFitSpline(sketch, "E382", {"points": [v(-39.18, -39.47) * mm, v(-39.02, -36.8) * mm, v(-38.38, -34.4) * mm, v(-37.26, -32.27) * mm]});
            skFitSpline(sketch, "E383", {"points": [v(-37.26, -32.27) * mm, v(-36.01, -29.87) * mm, v(-34.56, -28.6) * mm, v(-32.9, -28.47) * mm]});
            skFitSpline(sketch, "E384", {"points": [v(-33.16, -32.7) * mm, v(-33.78, -32.94) * mm, v(-34.35, -33.66) * mm, v(-34.85, -34.88) * mm]});
            skFitSpline(sketch, "E385", {"points": [v(-34.85, -34.88) * mm, v(-35.38, -36.2) * mm, v(-35.71, -37.8) * mm, v(-35.83, -39.7) * mm]});
            skFitSpline(sketch, "E386", {"points": [v(-35.83, -39.7) * mm, v(-35.93, -41.25) * mm, v(-35.82, -42.63) * mm, v(-35.5, -43.86) * mm]});
            skFitSpline(sketch, "E387", {"points": [v(-35.5, -43.86) * mm, v(-35.17, -45.25) * mm, v(-34.66, -46.06) * mm, v(-33.98, -46.3) * mm]});
            skFitSpline(sketch, "E388", {"points": [v(-33.22, -46.3) * mm, v(-32.6, -46) * mm, v(-32.05, -45.27) * mm, v(-31.56, -44.09) * mm]});
            skFitSpline(sketch, "E389", {"points": [v(-31.56, -44.09) * mm, v(-31.01, -42.81) * mm, v(-30.68, -41.27) * mm, v(-30.57, -39.45) * mm]});
            skFitSpline(sketch, "E390", {"points": [v(-30.57, -39.45) * mm, v(-30.41, -37) * mm, v(-30.75, -35) * mm, v(-31.56, -33.47) * mm]});
            skFitSpline(sketch, "E391", {"points": [v(-31.56, -33.47) * mm, v(-31.82, -33.02) * mm, v(-32.1, -32.75) * mm, v(-32.4, -32.65) * mm]});
            skFitSpline(sketch, "E392", {"points": [v(-32.15, -28.47) * mm, v(-30.32, -28.74) * mm, v(-28.92, -30.22) * mm, v(-27.95, -32.92) * mm]});
            skFitSpline(sketch, "E393", {"points": [v(-27.95, -32.92) * mm, v(-27.3, -35) * mm, v(-27.04, -37.17) * mm, v(-27.18, -39.44) * mm]});
            skFitSpline(sketch, "E394", {"points": [v(-27.18, -39.44) * mm, v(-27.34, -42.05) * mm, v(-27.99, -44.47) * mm, v(-29.12, -46.69) * mm]});
            skFitSpline(sketch, "E395", {"points": [v(-29.12, -46.69) * mm, v(-30.37, -49.15) * mm, v(-31.82, -50.46) * mm, v(-33.48, -50.64) * mm]});
            skFitSpline(sketch, "E396", {"points": [v(-7.58, -38.59) * mm, v(-7.05, -38.59) * mm, v(-6.6, -38.3) * mm, v(-6.25, -37.75) * mm]});
            skFitSpline(sketch, "E397", {"points": [v(-6.25, -37.75) * mm, v(-5.9, -37.2) * mm, v(-5.69, -36.5) * mm, v(-5.63, -35.64) * mm]});
            skFitSpline(sketch, "E398", {"points": [v(-5.63, -35.64) * mm, v(-5.59, -34.8) * mm, v(-5.7, -34.1) * mm, v(-6, -33.54) * mm]});
            skFitSpline(sketch, "E399", {"points": [v(-6, -33.54) * mm, v(-6.3, -32.96) * mm, v(-6.7, -32.68) * mm, v(-7.22, -32.68) * mm]});
            skFitSpline(sketch, "E400", {"points": [v(-6.42, -28.6) * mm, v(-5.33, -28.6) * mm, v(-4.42, -29.3) * mm, v(-3.7, -30.67) * mm]});
            skFitSpline(sketch, "E401", {"points": [v(-3.7, -30.67) * mm, v(-2.98, -32.06) * mm, v(-2.68, -33.68) * mm, v(-2.79, -35.53) * mm]});
            skFitSpline(sketch, "E402", {"points": [v(-2.79, -35.53) * mm, v(-2.89, -37.1) * mm, v(-3.22, -38.5) * mm, v(-3.79, -39.71) * mm]});
            skFitSpline(sketch, "E403", {"points": [v(-3.79, -39.71) * mm, v(-4.33, -40.94) * mm, v(-5.04, -41.8) * mm, v(-5.89, -42.28) * mm]});
            skFitSpline(sketch, "E404", {"points": [v(31.03, -28.6) * mm, v(33.86, -36.95) * mm, v(35.47, -41.7) * mm, v(35.85, -42.83) * mm]});
            skFitSpline(sketch, "E405", {"points": [v(46.25, -32.54) * mm, v(45.9, -32.63) * mm, v(45.58, -32.89) * mm, v(45.32, -33.31) * mm]});
            skFitSpline(sketch, "E406", {"points": [v(45.32, -33.31) * mm, v(45.06, -33.73) * mm, v(44.92, -34.16) * mm, v(44.9, -34.62) * mm]});
            skFitSpline(sketch, "E407", {"points": [v(44.9, -34.62) * mm, v(44.85, -35.5) * mm, v(45.22, -36.1) * mm, v(46, -36.44) * mm]});
            skFitSpline(sketch, "E408", {"points": [v(45.7, -41.61) * mm, v(44.11, -40.9) * mm, v(43.08, -40.07) * mm, v(42.59, -39.1) * mm]});
            skFitSpline(sketch, "E409", {"points": [v(42.59, -39.1) * mm, v(42.03, -38.02) * mm, v(41.8, -36.63) * mm, v(41.9, -34.92) * mm]});
            skFitSpline(sketch, "E410", {"points": [v(41.9, -34.92) * mm, v(42, -33.16) * mm, v(42.52, -31.67) * mm, v(43.44, -30.44) * mm]});
            skFitSpline(sketch, "E411", {"points": [v(43.44, -30.44) * mm, v(44.3, -29.3) * mm, v(45.32, -28.58) * mm, v(46.5, -28.3) * mm]});
            skFitSpline(sketch, "E412", {"points": [v(47.4, -28.24) * mm, v(49.41, -28.24) * mm, v(50.75, -29.51) * mm, v(51.4, -32.05) * mm]});
            skFitSpline(sketch, "E413", {"points": [v(48.97, -34.92) * mm, v(48.53, -33.76) * mm, v(47.87, -32.98) * mm, v(47, -32.58) * mm]});
            skFitSpline(sketch, "E414", {"points": [v(47.04, -36.88) * mm, v(48.55, -37.6) * mm, v(49.58, -38.26) * mm, v(50.1, -38.84) * mm]});
            skFitSpline(sketch, "E415", {"points": [v(50.1, -38.84) * mm, v(51.08, -39.95) * mm, v(51.5, -41.57) * mm, v(51.37, -43.72) * mm]});
            skFitSpline(sketch, "E416", {"points": [v(51.37, -43.72) * mm, v(51.23, -45.59) * mm, v(50.65, -47.16) * mm, v(49.6, -48.45) * mm]});
            skFitSpline(sketch, "E417", {"points": [v(49.6, -48.45) * mm, v(48.58, -49.71) * mm, v(47.35, -50.44) * mm, v(45.92, -50.62) * mm]});
            skFitSpline(sketch, "E418", {"points": [v(46.43, -46.34) * mm, v(46.97, -46.26) * mm, v(47.4, -46.06) * mm, v(47.7, -45.76) * mm]});
            skFitSpline(sketch, "E419", {"points": [v(47.7, -45.76) * mm, v(48, -45.43) * mm, v(48.18, -45.03) * mm, v(48.2, -44.54) * mm]});
            skFitSpline(sketch, "E420", {"points": [v(48.2, -44.54) * mm, v(48.28, -43.39) * mm, v(47.78, -42.57) * mm, v(46.73, -42.08) * mm]});
            skFitSpline(sketch, "E421", {"points": [v(46.73, -42.08) * mm, v(46.55, -42) * mm, v(46.45, -41.94) * mm, v(46.45, -41.93) * mm]});
            skFitSpline(sketch, "E422", {"points": [v(45.15, -50.68) * mm, v(43.98, -50.61) * mm, v(42.97, -50.12) * mm, v(42.11, -49.2) * mm]});
            skFitSpline(sketch, "E423", {"points": [v(42.11, -49.2) * mm, v(41.27, -48.3) * mm, v(40.71, -47.11) * mm, v(40.42, -45.62) * mm]});
            skFitSpline(sketch, "E424", {"points": [v(43.58, -43.02) * mm, v(43.64, -44.75) * mm, v(44.26, -45.81) * mm, v(45.42, -46.23) * mm]});
            skSolve(sketch);
        }
        {
            var Q0;
            Q0=makeQuery(id+"F0.imprint","IMPRINT",FACE,{"disambiguationData":[TD([[makeQuery(id+"F0.imprint","IMPRINT",EDGE,{"derivedFrom":sQuery(id+"F0.wireOp",EDGE,"E0")}),-1.0]])]});
            extrude(context, id + "F1", {"entities" : qUnion([Q0]), "depth" : 2 * mm, "offsetDistance" : 25 * mm});
        }
    });
